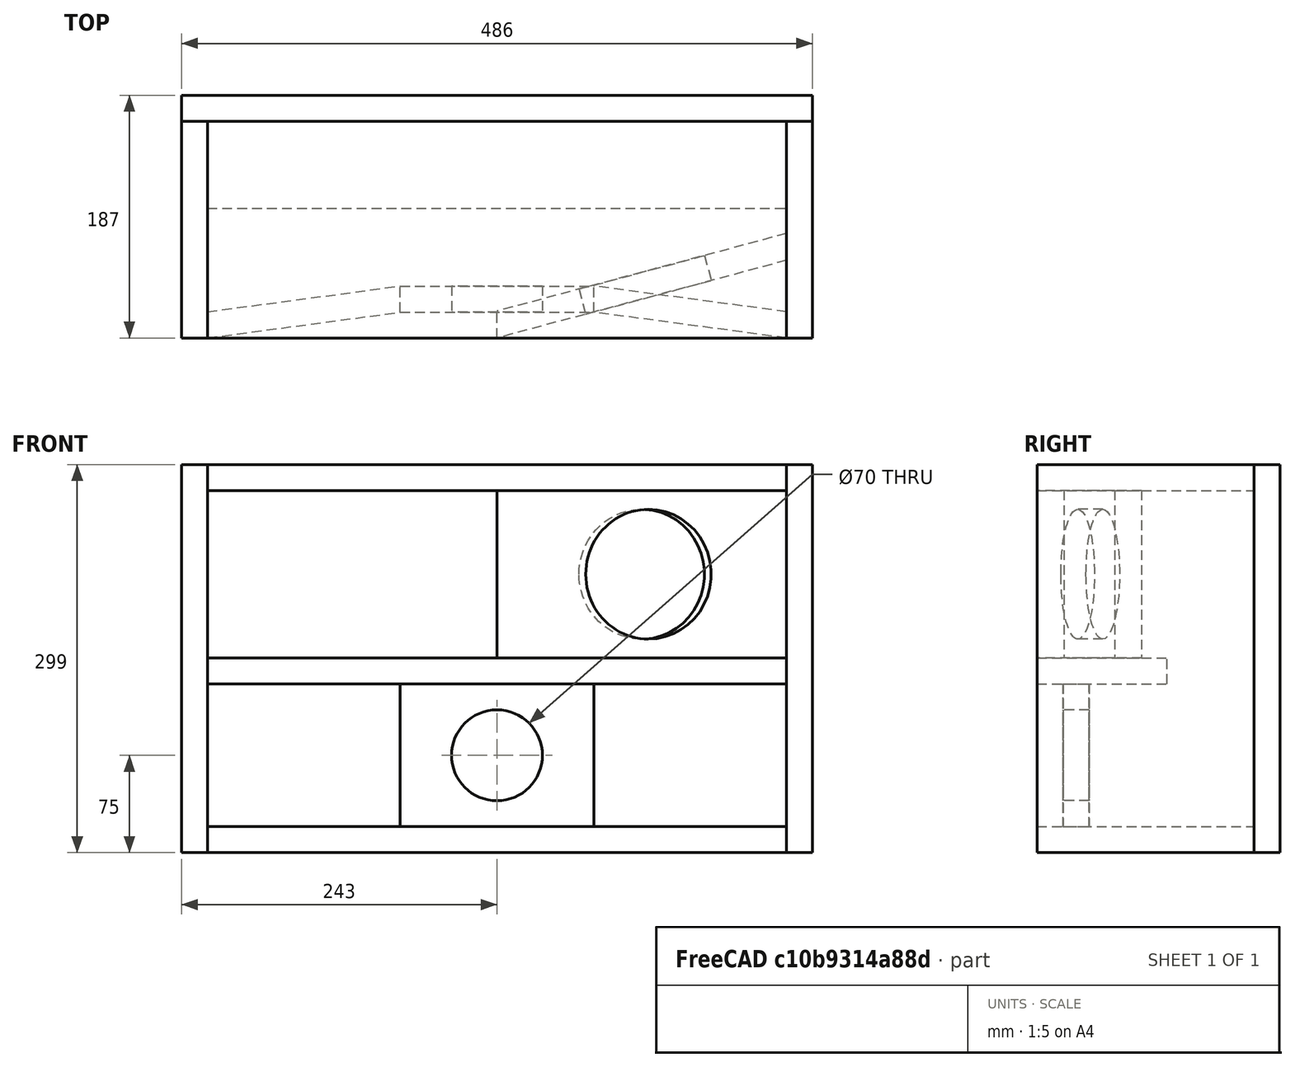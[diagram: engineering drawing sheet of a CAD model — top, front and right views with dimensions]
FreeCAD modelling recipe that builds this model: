
FCSTD DOCUMENT  (FreeCAD 0.17R13541 (Git))
Label: designEnceinteFreeCAD
License: All rights reserved
LicenseURL: http://en.wikipedia.org/wiki/All_rights_reserved
objects: Part::Box×16, Part::Cut×8, Part::Cylinder×2, Part::Mirroring×2
note: 28 computed .brp shape members not serialized (recipe doc carries the construction recipe); baked Part::Feature solids carry a one-line shape summary decoded from their .brp

FEATURE [Part::Box] Box  label="Face gauche"
  AttacherType = Attacher::AttachEngine3D
  Height = 299
  Length = 20
  Placement = pos=(-243,-20,-214.5) rot=(0,0,1;0rad)
  Width = 167
FEATURE [Part::Box] Box001  label="Face droite"
  AttacherType = Attacher::AttachEngine3D
  Height = 299
  Length = 20
  Placement = pos=(223,-20,-214.5) rot=(0,0,1;0rad)
  Width = 167
FEATURE [Part::Box] Box002  label="Face haute"
  AttacherType = Attacher::AttachEngine3D
  Height = 20
  Length = 446
  Placement = pos=(-223,-20,64.5) rot=(0,0,1;0rad)
  Width = 167
FEATURE [Part::Box] Box003  label="Face fond"
  AttacherType = Attacher::AttachEngine3D
  Height = 299
  Length = 486
  Placement = pos=(-243,147,-214.5) rot=(0,0,1;0rad)
  Width = 20
FEATURE [Part::Box] Box004  label="Face basse"
  AttacherType = Attacher::AttachEngine3D
  Height = 20
  Length = 446
  Placement = pos=(-223,-20,-214.5) rot=(0,0,1;0rad)
  Width = 167
FEATURE [Part::Box] Box005  label="Face bass reflex"
  AttacherType = Attacher::AttachEngine3D
  Height = 110
  Length = 149
  Placement = pos=(-74.5,0,-194.5) rot=(0,0,1;0rad)
  Width = 20
FEATURE [Part::Box] Box006  label="Face intermédiaire"
  AttacherType = Attacher::AttachEngine3D
  Height = 20
  Length = 446
  Placement = pos=(-223,-20,-84.5) rot=(0,0,1;0rad)
  Width = 100
FEATURE [Part::Cylinder] Cylinder  label="Bass Reflex"
  Angle = 360
  AttacherType = Attacher::AttachEngine3D
  Height = 115
  Placement = pos=(0,115,-139.5) rot=(1,0,0;1.5708rad)
  Radius = 35
FEATURE [Part::Cut] Cut  label="Avant Bass Reflex"
  Base = -> Box005
  Tool = -> Cylinder
FEATURE [Part::Box] Box007  label="Face avant gauche"
  AttacherType = Attacher::AttachEngine3D
  Height = 110
  Length = 153
  Placement = pos=(-223,-20,-194.5) rot=(0,0,1;0.132645rad)
  Width = 20
FEATURE [Part::Box] Box008  label="Coupe1"
  AttacherType = Attacher::AttachEngine3D
  Height = 110
  Length = 10
  Placement = pos=(-74.5,-1,-194.5) rot=(0,0,1;0rad)
  Width = 23
FEATURE [Part::Box] Box009  label="Coupe2"
  AttacherType = Attacher::AttachEngine3D
  Height = 110
  Length = 20
  Placement = pos=(-243,-20,-194.5) rot=(0,0,1;0rad)
  Width = 21
FEATURE [Part::Cut] Cut001
  Base = -> Box007
  Tool = -> Box009
FEATURE [Part::Cut] Cut002  label="Coupe avant gauche"
  Base = -> Cut001
  Refine = true
  Tool = -> Box008
FEATURE [Part::Box] Box010  label="Face avant gauche001"
  AttacherType = Attacher::AttachEngine3D
  Height = 110
  Length = 153
  Placement = pos=(-223,-20,-194.5) rot=(0,0,1;0.132645rad)
  Width = 20
FEATURE [Part::Box] Box011  label="Coupe003"
  AttacherType = Attacher::AttachEngine3D
  Height = 110
  Length = 20
  Placement = pos=(-243,-20,-194.5) rot=(0,0,1;0rad)
  Width = 21
FEATURE [Part::Box] Box012  label="Coupe004"
  AttacherType = Attacher::AttachEngine3D
  Height = 110
  Length = 10
  Placement = pos=(-74.5,-1,-194.5) rot=(0,0,1;0rad)
  Width = 23
FEATURE [Part::Cut] Cut004
  Base = -> Box010
  Tool = -> Box011
FEATURE [Part::Cut] Cut003  label="Coupe avant droit"
  Base = -> Cut004
  Tool = -> Box012
FEATURE [Part::Mirroring] Part__Mirroring  label="Coupe avant droit001"
  Base = (0,0,0)
  Normal = (1,0,0)
  Source = -> Cut003
FEATURE [Part::Box] Box014  label="Cube001"
  AttacherType = Attacher::AttachEngine3D
  Height = 129
  Length = 10
  Placement = pos=(0,-21,-64.5) rot=(0,0,1;0rad)
  Width = 30
FEATURE [Part::Box] Box016  label="Cube003"
  AttacherType = Attacher::AttachEngine3D
  Height = 129
  Length = 7
  Placement = pos=(-230,39,-64.5) rot=(0,0,1;0rad)
  Width = 23
FEATURE [Part::Box] Box017  label="Cube"
  AttacherType = Attacher::AttachEngine3D
  Height = 129
  Length = 237
  Placement = pos=(-110.5,0,-64.5) rot=(0,0,1;0rad)
  Width = 20
FEATURE [Part::Cylinder] Cylinder001  label="Cylindre"
  Angle = 360
  AttacherType = Attacher::AttachEngine3D
  Height = 20
  Placement = pos=(5,20,0) rot=(1,0,0;1.5708rad)
  Radius = 50
FEATURE [Part::Cut] Cut005
  Base = -> Box017
  Placement = pos=(-121.5,12.56,0) rot=(0,0,-1;0.261799rad)
  Tool = -> Cylinder001
FEATURE [Part::Cut] Cut006
  Base = -> Cut005
  Tool = -> Box014
FEATURE [Part::Cut] Cut007  label="HP Gauche"
  Base = -> Cut006
  Tool = -> Box016
FEATURE [Part::Mirroring] Part__Mirroring001  label="HP droit"
  Base = (0,0,0)
  Normal = (1,0,0)
  Source = -> Cut007
